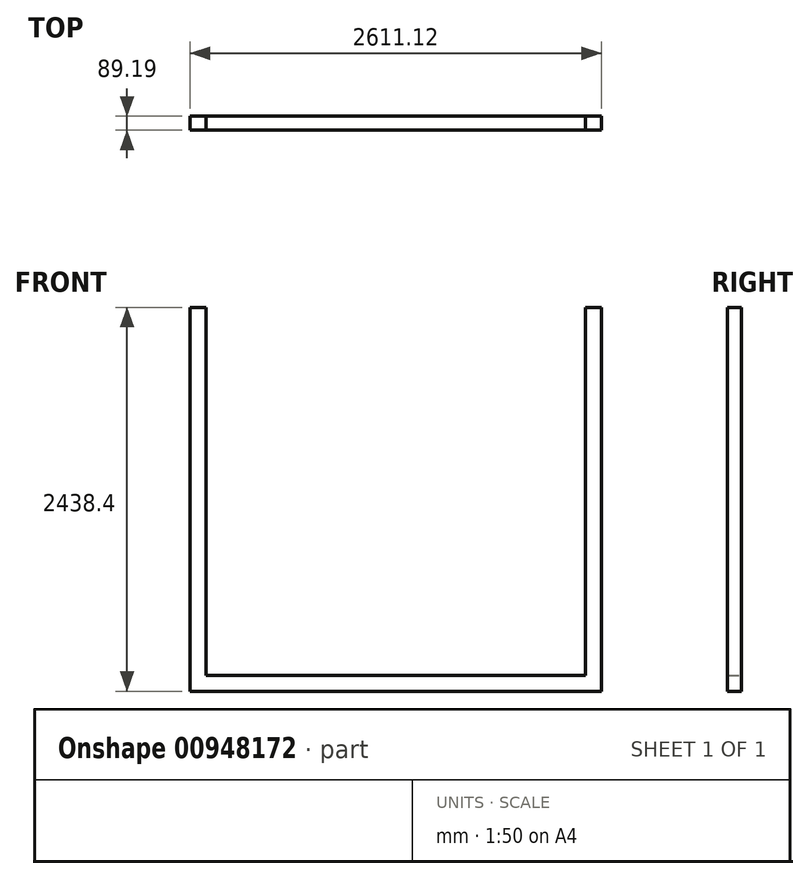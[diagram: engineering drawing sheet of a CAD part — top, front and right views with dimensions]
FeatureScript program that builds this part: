
annotation { "Feature Type Name" : "Feature", "Feature Type Description" : "" }
export const myFeature = defineFeature(function(context is Context, id is Id, definition is map)
    precondition{}
    {
        {
            var Q0;
            Q0=qCreatedBy(makeId("Front.planeOp"),FACE);
            var sketch = newSketch(context, id + "F0", { "sketchPlane" : qUnion([Q0])});
            skLineSegment(sketch, "E0.bottom", {"start": v(-1467.32, 1131.88) * mm, "end": v(-1365.72, 1131.88) * mm});
            skLineSegment(sketch, "E0.top", {"start": v(-1467.32, -1306.52) * mm, "end": v(-1365.72, -1306.52) * mm});
            skLineSegment(sketch, "E0.left", {"start": v(-1467.32, 1131.88) * mm, "end": v(-1467.32, -1306.52) * mm});
            skLineSegment(sketch, "E0.right", {"start": v(-1365.72, 1131.88) * mm, "end": v(-1365.72, -1306.52) * mm});
            skLineSegment(sketch, "E1.bottom", {"start": v(-1365.72, -1306.52) * mm, "end": v(1042.2, -1306.52) * mm});
            skLineSegment(sketch, "E1.top", {"start": v(-1365.72, -1204.92) * mm, "end": v(1042.2, -1204.92) * mm});
            skLineSegment(sketch, "E1.left", {"start": v(-1365.72, -1306.52) * mm, "end": v(-1365.72, -1204.92) * mm});
            skLineSegment(sketch, "E1.right", {"start": v(1042.2, -1306.52) * mm, "end": v(1042.2, -1204.92) * mm});
            skLineSegment(sketch, "E2.bottom", {"start": v(1143.8, -1306.52) * mm, "end": v(1042.2, -1306.52) * mm});
            skLineSegment(sketch, "E2.top", {"start": v(1143.8, 1131.88) * mm, "end": v(1042.2, 1131.88) * mm});
            skLineSegment(sketch, "E2.left", {"start": v(1143.8, -1306.52) * mm, "end": v(1143.8, 1131.88) * mm});
            skLineSegment(sketch, "E2.right", {"start": v(1042.2, -1306.52) * mm, "end": v(1042.2, 1131.88) * mm});
            skSolve(sketch);
        }
        {
            var Q0;
            Q0=makeQuery(id+"F0.imprint","IMPRINT",FACE,{"disambiguationData":[TD([[makeQuery(id+"F0.imprint","IMPRINT",EDGE,{"derivedFrom":sQuery(id+"F0.wireOp",EDGE,"E0.bottom")}),-1.0]])]});
            var Q1;
            {var subQ0=sQuery(id+"F0.wireOp",EDGE,"E1.bottom");Q1=makeQuery(id+"F0.imprint","IMPRINT",FACE,{"disambiguationData":[TD([[makeQuery(id+"F0.imprint","IMPRINT",EDGE,{"derivedFrom":subQ0}),1.0]])]});}
            var Q2;
            {var subQ1=sQuery(id+"F0.wireOp",EDGE,"E2.bottom");Q2=makeQuery(id+"F0.imprint","IMPRINT",FACE,{"disambiguationData":[TD([[makeQuery(id+"F0.imprint","IMPRINT",EDGE,{"derivedFrom":subQ1}),-1.0]])]});}
            extrude(context, id + "F1", {"entities" : qUnion([Q0, Q1, Q2]), "depth" : 89.19 * mm, "offsetDistance" : 25.4 * mm});
        }
    });
